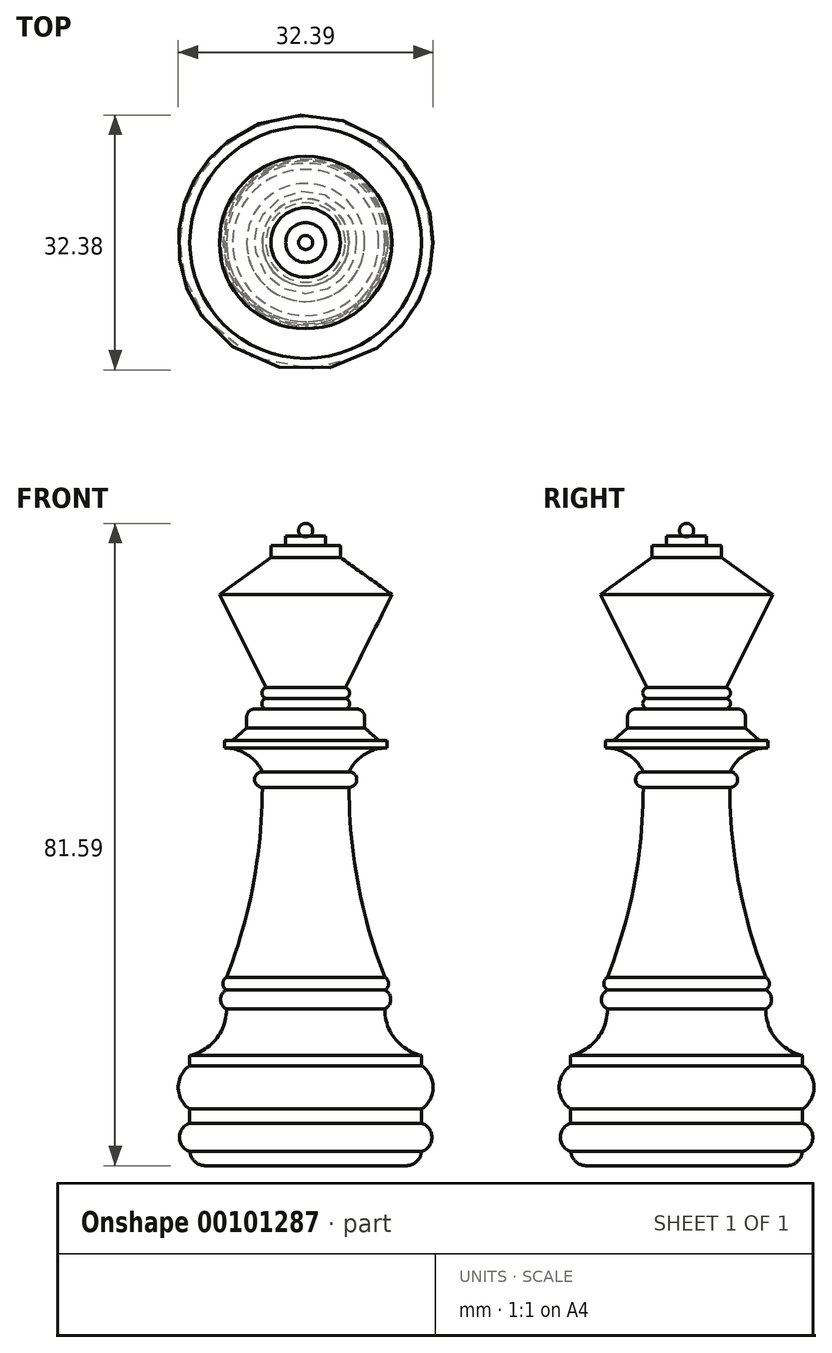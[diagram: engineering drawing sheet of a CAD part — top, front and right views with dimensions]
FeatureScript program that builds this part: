
annotation { "Feature Type Name" : "Feature", "Feature Type Description" : "" }
export const myFeature = defineFeature(function(context is Context, id is Id, definition is map)
    precondition{}
    {
        {
            var Q0;
            Q0=qCreatedBy(makeId("Front.planeOp"),FACE);
            var sketch = newSketch(context, id + "F0", { "sketchPlane" : qUnion([Q0])});
            skLineSegment(sketch, "E0", {"start": v(-203.37, 101.25) * mm, "end": v(-203.37, 21.25) * mm});
            skLineSegment(sketch, "E1", {"start": v(-203.37, 21.25) * mm, "end": v(-188.64, 21.25) * mm});
            skLineSegment(sketch, "E2", {"start": v(-188.64, 21.25) * mm, "end": v(-188.64, 23.04) * mm});
            skArc(sketch, "E3", {"start": v(-188.64, 23.04) * mm, "mid": v(-187.33, 24.85) * mm, "end": v(-188.64, 26.65) * mm});
            skLineSegment(sketch, "E4", {"start": v(-188.64, 26.65) * mm, "end": v(-188.64, 28.44) * mm});
            skArc(sketch, "E5", {"start": v(-188.64, 28.44) * mm, "mid": v(-187.17, 31.2) * mm, "end": v(-188.64, 33.94) * mm});
            skLineSegment(sketch, "E6", {"start": v(-188.64, 33.94) * mm, "end": v(-188.64, 35.24) * mm});
            skLineSegment(sketch, "E7", {"start": v(-188.64, 35.24) * mm, "end": v(-193.3, 35.24) * mm});
            skLineSegment(sketch, "E8", {"start": v(-193.3, 35.24) * mm, "end": v(-193.3, 41.17) * mm});
            skArc(sketch, "E9", {"start": v(-193.3, 41.17) * mm, "mid": v(-192.56, 42.37) * mm, "end": v(-193.3, 43.57) * mm});
            skArc(sketch, "E10", {"start": v(-193.3, 43.57) * mm, "mid": v(-192.84, 44.37) * mm, "end": v(-193.3, 45.17) * mm});
            skLineSegment(sketch, "E11", {"start": v(-197.86, 69.31) * mm, "end": v(-197.86, 45.17) * mm});
            skLineSegment(sketch, "E12", {"start": v(-197.86, 45.17) * mm, "end": v(-193.3, 45.17) * mm});
            skArc(sketch, "E13", {"start": v(-197.86, 69.31) * mm, "mid": v(-196.88, 70.3) * mm, "end": v(-197.86, 71.28) * mm});
            skLineSegment(sketch, "E14", {"start": v(-197.86, 71.28) * mm, "end": v(-197.86, 74.33) * mm});
            skLineSegment(sketch, "E15", {"start": v(-197.86, 74.33) * mm, "end": v(-193.04, 74.33) * mm});
            skLineSegment(sketch, "E16", {"start": v(-193.04, 74.33) * mm, "end": v(-193.04, 75.27) * mm});
            skLineSegment(sketch, "E17", {"start": v(-193.04, 75.27) * mm, "end": v(-194.08, 75.27) * mm});
            skLineSegment(sketch, "E18", {"start": v(-194.08, 75.27) * mm, "end": v(-195.87, 76.85) * mm});
            skLineSegment(sketch, "E19", {"start": v(-195.87, 76.85) * mm, "end": v(-195.87, 79.26) * mm});
            skLineSegment(sketch, "E20", {"start": v(-195.87, 79.26) * mm, "end": v(-198.32, 79.26) * mm});
            skArc(sketch, "E21", {"start": v(-198.32, 79.26) * mm, "mid": v(-197.8, 79.94) * mm, "end": v(-198.32, 80.62) * mm});
            skLineSegment(sketch, "E22", {"start": v(-198.32, 81.98) * mm, "end": v(-192.4, 93.8) * mm});
            skLineSegment(sketch, "E23", {"start": v(-192.4, 93.8) * mm, "end": v(-198.95, 98.5) * mm});
            skLineSegment(sketch, "E24", {"start": v(-198.95, 98.5) * mm, "end": v(-198.95, 100.03) * mm});
            skLineSegment(sketch, "E25", {"start": v(-198.95, 100.03) * mm, "end": v(-200.83, 100.03) * mm});
            skLineSegment(sketch, "E26", {"start": v(-200.83, 100.03) * mm, "end": v(-200.83, 101.25) * mm});
            skLineSegment(sketch, "E27", {"start": v(-200.83, 101.25) * mm, "end": v(-203.37, 101.25) * mm});
            skArc(sketch, "E28", {"start": v(-198.32, 80.62) * mm, "mid": v(-197.8, 81.3) * mm, "end": v(-198.32, 81.98) * mm});
            skSolve(sketch);
        }
        {
            var Q0;
            Q0=makeQuery(id+"F0.imprint","IMPRINT",FACE,{"disambiguationData":[TD([[makeQuery(id+"F0.imprint","IMPRINT",EDGE,{"derivedFrom":sQuery(id+"F0.wireOp",EDGE,"E0")}),1.0]])]});
            var Q1;
            Q1=sQuery(id+"F0.wireOp",EDGE,"E0");
            revolve(context, id + "F1", {"entities" : qUnion([Q0]), "axis" : qUnion([Q1]), "revolveType" : RevolveType.FULL});
        }
        {
            var Q0;
            Q0=makeQuery(id+"F1.opRevolve","SWEPT_EDGE",EDGE,{"disambiguationData":[OSD([sQuery(id+"F0.wireOp",EDGE,"E1"),sQuery(id+"F0.wireOp",EDGE,"E2")])]});
            fillet(context, id + "F2", {"entities" : qUnion([Q0]), "radius" : 2 * mm, "tangentPropagation" : true, "allowEdgeOverflow" : false});
        }
        {
            var Q0;
            Q0=makeQuery(id+"F1.opRevolve","SWEPT_EDGE",EDGE,{"disambiguationData":[OSD([sQuery(id+"F0.wireOp",EDGE,"E7"),sQuery(id+"F0.wireOp",EDGE,"E8")])]});
            var Q1;
            Q1=makeQuery(id+"F4.opFillet","BLEND_FACE",FACE,{"disambiguationData":[OSD([sQuery(id+"F0.wireOp",EDGE,"E11"),sQuery(id+"F0.wireOp",EDGE,"E12")])]});
            fillet(context, id + "F3", {"entities" : qUnion([Q0, Q1]), "radius" : 6 * mm, "tangentPropagation" : true, "allowEdgeOverflow" : false});
        }
        {
            var Q0;
            Q0=makeQuery(id+"F1.opRevolve","SWEPT_EDGE",EDGE,{"disambiguationData":[OSD([sQuery(id+"F0.wireOp",EDGE,"E11"),sQuery(id+"F0.wireOp",EDGE,"E12")])]});
            fillet(context, id + "F4", {"entities" : qUnion([Q0]), "radius" : 66.3 * mm, "tangentPropagation" : true, "allowEdgeOverflow" : false});
        }
        {
            var Q0;
            Q0=makeQuery(id+"F1.opRevolve","SWEPT_EDGE",EDGE,{"disambiguationData":[OSD([sQuery(id+"F0.wireOp",EDGE,"E14"),sQuery(id+"F0.wireOp",EDGE,"E15")])]});
            fillet(context, id + "F5", {"entities" : qUnion([Q0]), "radius" : 5.33 * mm, "tangentPropagation" : true, "allowEdgeOverflow" : false});
        }
        {
            var Q0;
            Q0=makeQuery(id+"F1.opRevolve","SWEPT_EDGE",EDGE,{"disambiguationData":[OSD([sQuery(id+"F0.wireOp",EDGE,"E19"),sQuery(id+"F0.wireOp",EDGE,"E20")])]});
            fillet(context, id + "F6", {"entities" : qUnion([Q0]), "radius" : 1 * mm, "tangentPropagation" : true, "allowEdgeOverflow" : false});
        }
        {
            var Q0;
            Q0=makeQuery(id+"F1.opRevolve","SWEPT_FACE",FACE,{"disambiguationData":[OSD([sQuery(id+"F0.wireOp",EDGE,"E27")])]});
            cPlane(context, id + "F7", {"entities" : qUnion([Q0]), "cplaneType" : CPlaneType.OFFSET, "offset" : 0.2 * mm, "oppositeDirection" : true, "width" : 150 * mm, "height" : 150 * mm});
        }
        {
            var Q0;
            Q0=qCreatedBy(id+"F7.planeOp",FACE);
            var sketch = newSketch(context, id + "F8", { "sketchPlane" : qUnion([Q0])});
            skPoint(sketch, "E29.middle", {"position": v(-203.37, 0) * mm});
            skCircle(sketch, "E30", {"center": v(-203.37, 0) * mm, "radius": 0.9 * mm});
            skSolve(sketch);
        }
        {
            var Q0;
            Q0=makeQuery(id+"F8.imprint","IMPRINT",FACE,{"disambiguationData":[TD([[makeQuery(id+"F8.imprint","IMPRINT",EDGE,{"derivedFrom":sQuery(id+"F8.wireOp",EDGE,"E30")}),1.0]])]});
            extrude(context, id + "F9", {"entities" : qUnion([Q0]), "depth" : 1.8 * mm});
        }
        {
            var Q0;
            Q0=makeQuery(id+"F9.opExtrude","CAP_EDGE",EDGE,{"disambiguationData":[OSD([sQuery(id+"F8.wireOp",EDGE,"E30")])],"isStart":false});
            var Q1;
            Q1=makeQuery(id+"F9.opExtrude","CAP_EDGE",EDGE,{"disambiguationData":[OSD([sQuery(id+"F8.wireOp",EDGE,"E30")])],"isStart":true});
            fillet(context, id + "F10", {"entities" : qUnion([Q0, Q1]), "radius" : 0.9 * mm, "tangentPropagation" : true, "allowEdgeOverflow" : false});
        }
    });
